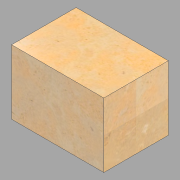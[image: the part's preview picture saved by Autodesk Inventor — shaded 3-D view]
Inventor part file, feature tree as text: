
AUTODESK INVENTOR PART (.ipt)
format: ipt  version: 2022.1 (Build 261234020, 234B)  size: 128,000 bytes
history: native  units: in
note: dims shown in document units (in); Inventor stores cm internally (conversion verified against a paired STEP export)
features: extrude x1, sketch x1
ambient origin geometry x8: Origin, YZ Plane, XZ Plane, XY Plane, X Axis, Y Axis, Z Axis, Center Point
bodies: Solid1 (feature_tree)
feature tree (2):
  extrude  "Extrusion1"  Depth=3.5in
  sketch  "Sketch1"  dims[d0=3.5in d1=3.5in d2=5.0in d3=0.0in]
